# Revit family: Electronics_Visual-Projectors_ViewSonic_The-ViewSonicR-PRO9800WUL-Projector
name_source: partatom
category: Electrical Equipment
revit_build: Autodesk Revit 2015 (Build: 20140606_1530(x64)
units: mm (PartAtom-declared; Revit-internal decimal feet)

## types (1)
- 9800WUL
    Assembly Code = D50
    BIMobject category = Visual - Projectors
    BIMobject category code = electronics-visual-projectors
    BIMobject main category = Electronics
    BIMobject main category code = electronics
    BOSUseNativeGeometries = 1
    Brand url = https://www.viewsonic.com
    Covering Color = Plastic - Viewsonic - White
    Description = Bright and versatile for any professional installation, the ViewSonic® Pro9800WUL WUXGA projector delivers everything you need for big screens in big venues. Delivering 5,500 lumens of advanced high brightness, this projector is ideal for auditoriums, large boardrooms, houses of worship, and more. Thanks to SuperColor™ technology, content is brought to life with captivating color, crisp graphics, and stunning videos no matter the environment. Designed for installers, this top-notch performer is also easy to deploy and manage with its wide 1.7x optical zoom adjustment, a centered lens design, and a vertical/horizontal lens shift feature that provides extreme flexibility in even the most challenging installations. Thanks to the stackable design of these projectors, light output can be doubled by simply placing one projector on top of the other - perfect for large venues with high ambient light.
    Design country = Taiwan
    Edition number = 1
    Keynote = V90
    Manufacturer = ViewSonic
    Manufacturer country = Taiwan
    Manufacturer name = ViewSonic
    Model = viewsonic_9800wul
    Product Guid = bee1d77a-7752-484a-95a9-d481cab154b7
    Product SKU = viewsonic_9800WUL
    Product data url = https://bimobject.com
    Product family = Electronics
    Product group = Projectors
    Product name = The ViewSonic® 9800WUL Projector
    Product url = https://www.viewsonic.com
    QR code = http://bimobject.com
    URL = www.viewsonic.com
    a = Image Aspect Ratio : "4  - 3"
    b = Image Aspect Ratio : "16 - 9"
    c = Image Aspect Ratio : "16 - 10"

## geometry (parser evidence)
native form markers: Blend x2, Sweep x7
no freeform markers — native parametric forms only
